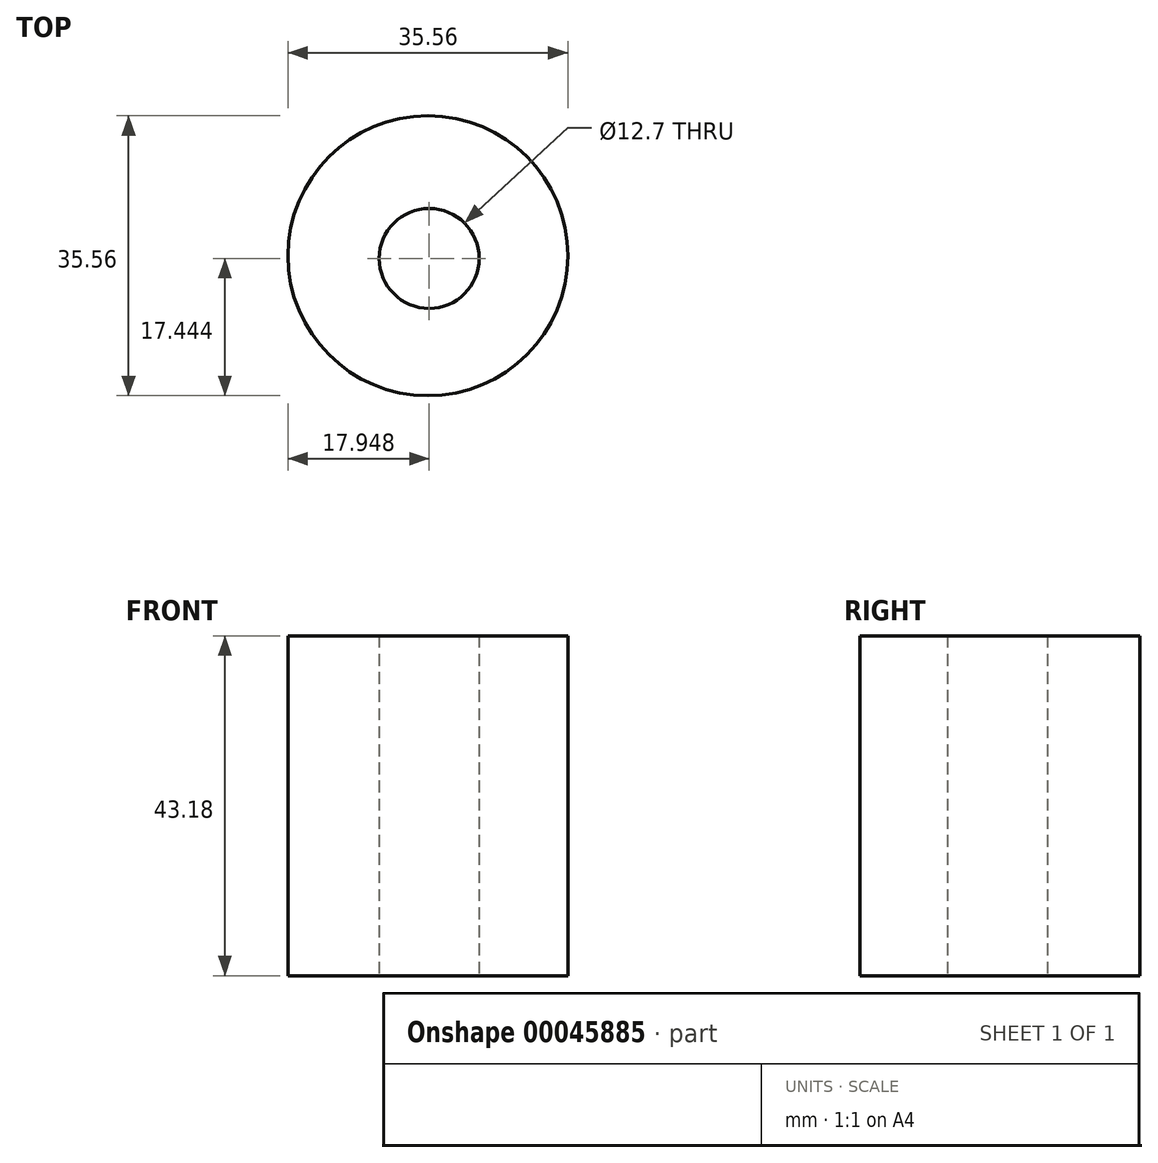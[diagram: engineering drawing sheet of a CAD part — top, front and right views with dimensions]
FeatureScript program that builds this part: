
annotation { "Feature Type Name" : "Feature", "Feature Type Description" : "" }
export const myFeature = defineFeature(function(context is Context, id is Id, definition is map)
    precondition{}
    {
        {
            var Q0;
            Q0=qCreatedBy(makeId("Top.planeOp"),FACE);
            var sketch = newSketch(context, id + "F0", { "sketchPlane" : qUnion([Q0])});
            skCircle(sketch, "E0", {"center": v(0, 0) * mm, "radius": 17.78 * mm});
            skCircle(sketch, "E1", {"center": v(0.17, -0.34) * mm, "radius": 6.35 * mm});
            skSolve(sketch);
        }
        {
            var Q0;
            Q0=makeQuery(id+"F0.imprint","IMPRINT",FACE,{"disambiguationData":[TD([[makeQuery(id+"F0.imprint","IMPRINT",EDGE,{"derivedFrom":sQuery(id+"F0.wireOp",EDGE,"E0")}),1.0]])]});
            extrude(context, id + "F1", {"entities" : qUnion([Q0]), "depth" : 43.18 * mm});
        }
    });
